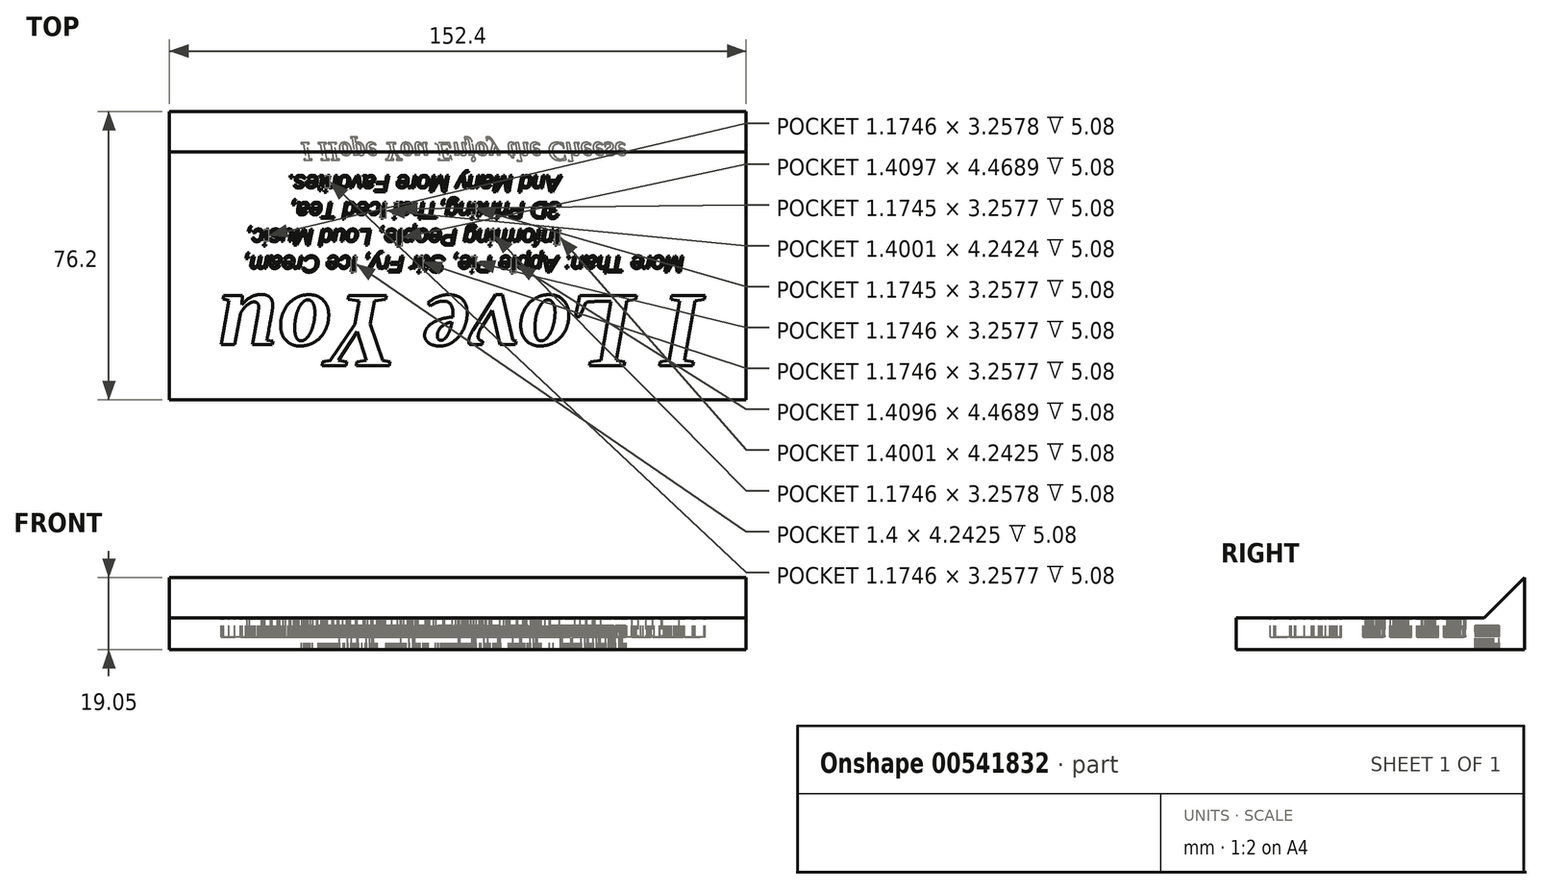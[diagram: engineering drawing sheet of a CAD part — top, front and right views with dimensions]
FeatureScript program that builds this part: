
annotation { "Feature Type Name" : "Feature", "Feature Type Description" : "" }
export const myFeature = defineFeature(function(context is Context, id is Id, definition is map)
    precondition{}
    {
        {
            var Q0;
            Q0=qCreatedBy(makeId("Top.planeOp"),FACE);
            var sketch = newSketch(context, id + "F0", { "sketchPlane" : qUnion([Q0])});
            skLineSegment(sketch, "E0", {"start": v(0, 0) * mm, "end": v(76.2, 0) * mm});
            skLineSegment(sketch, "E1", {"start": v(76.2, 0) * mm, "end": v(76.2, 76.2) * mm});
            skLineSegment(sketch, "E2", {"start": v(76.2, 76.2) * mm, "end": v(-76.2, 76.2) * mm});
            skLineSegment(sketch, "E3", {"start": v(-76.2, 76.2) * mm, "end": v(-76.2, 0) * mm});
            skLineSegment(sketch, "E4", {"start": v(-76.2, 0) * mm, "end": v(0, 0) * mm});
            skSolve(sketch);
        }
        {
            var Q0;
            Q0 = qSketchRegion(id + "F0", true);
            extrude(context, id + "F1", {"entities" : qUnion([Q0]), "depth" : 8.38 * mm, "offsetDistance" : 25.4 * mm});
        }
        {
            var Q0;
            Q0=makeQuery(id+"F1.opExtrude","SWEPT_FACE",FACE,{"disambiguationData":[OSD([sQuery(id+"F0.wireOp",EDGE,"E3")])]});
            var sketch = newSketch(context, id + "F2", { "sketchPlane" : qUnion([Q0])});
            skLineSegment(sketch, "E5", {"start": v(0, 0) * mm, "end": v(0, 19.05) * mm});
            skLineSegment(sketch, "E6", {"start": v(0, 19.05) * mm, "end": v(-19.05, 0) * mm});
            skLineSegment(sketch, "E7", {"start": v(-19.05, 0) * mm, "end": v(0, 0) * mm});
            skSolve(sketch);
        }
        {
            var Q0;
            Q0 = qSketchRegion(id + "F2", true);
            extrude(context, id + "F3", {"entities" : qUnion([Q0]), "operationType" : NewBodyOperationType.ADD, "oppositeDirection" : true, "depth" : 152.4 * mm, "offsetDistance" : 25.4 * mm});
        }
        {
            var Q0;
            Q0=makeQuery(id+"F1.opExtrude","CAP_FACE",FACE,{"disambiguationData":[OSD([sQuery(id+"F0.wireOp",EDGE,"E0"),sQuery(id+"F0.wireOp",EDGE,"E1"),sQuery(id+"F0.wireOp",EDGE,"E2"),sQuery(id+"F0.wireOp",EDGE,"E3"),sQuery(id+"F0.wireOp",EDGE,"E4")])],"isStart":false});
            var sketch = newSketch(context, id + "F4", { "sketchPlane" : qUnion([Q0])});
            skText(sketch, "E8", { "text": "I Love You", "fontName": "Tinos-BoldItalic.ttf"});
            const initialGuessF4  = {"E8": [-0.06505, 0.0487, 1, 0, 0.02032]};
            skSetInitialGuess(sketch, initialGuessF4);
            skSolve(sketch);
        }
        {
            var Q0;
            Q0 = qSketchRegion(id + "F4", true);
            extrude(context, id + "F5", {"entities" : qUnion([Q0]), "operationType" : NewBodyOperationType.REMOVE, "oppositeDirection" : true, "depth" : 5.08 * mm, "offsetDistance" : 25.4 * mm});
        }
        {
            var Q0;
            {var subQ0=sQuery(id+"F0.wireOp",EDGE,"E3");var subQ1=sQuery(id+"F0.wireOp",EDGE,"E2");var subQ5=sQuery(id+"F0.wireOp",EDGE,"E1");Q0=makeQuery(id+"F5.boolean.opBoolean","SPLIT",FACE,{"disambiguationData":[TD([makeQuery(id+"F1.opExtrude","SWEPT_FACE",FACE,{"disambiguationData":[OSD([subQ5])]})])],"derivedFrom":makeQuery(id+"F1.opExtrude","CAP_FACE",FACE,{"disambiguationData":[OSD([sQuery(id+"F0.wireOp",EDGE,"E0"),subQ5,subQ1,subQ0,sQuery(id+"F0.wireOp",EDGE,"E4")])],"isStart":false})});}
            var sketch = newSketch(context, id + "F6", { "sketchPlane" : qUnion([Q0])});
            skText(sketch, "E9", { "text": "More Than: Apple Pie, Stir Fry, Ice Cream,\n                   Informing People, Loud Music,\n                   3D Printing,Thai Iced Tea,\n                   And Many More Favorites.", "fontName": "Arimo-Italic.ttf"});
            const initialGuessF6  = {"E9": [-0.05977, 0.0382, 1, 0, 0.00444]};
            skSetInitialGuess(sketch, initialGuessF6);
            skSolve(sketch);
        }
        {
            var Q0;
            Q0 = qSketchRegion(id + "F6", true);
            extrude(context, id + "F7", {"entities" : qUnion([Q0]), "operationType" : NewBodyOperationType.REMOVE, "oppositeDirection" : true, "depth" : 5.08 * mm, "offsetDistance" : 25.4 * mm});
        }
        {
            var Q0;
            Q0=makeQuery(id+"F1.opExtrude","SWEPT_BODY",BODY,{"disambiguationData":[OSD([sQuery(id+"F0.wireOp",EDGE,"E0"),sQuery(id+"F0.wireOp",EDGE,"E1"),sQuery(id+"F0.wireOp",EDGE,"E2"),sQuery(id+"F0.wireOp",EDGE,"E3"),sQuery(id+"F0.wireOp",EDGE,"E4")])]});
            var Q1;
            Q1=makeQuery(id+"F3.boolean.opBoolean","MERGE",EDGE,{"derivedFrom":[makeQuery(id+"F1.opExtrude","SWEPT_EDGE",EDGE,{"disambiguationData":[OSD([sQuery(id+"F0.wireOp",EDGE,"E0"),sQuery(id+"F0.wireOp",EDGE,"E1")])]}),makeQuery(id+"F3.opExtrude","CAP_EDGE",EDGE,{"disambiguationData":[OSD([sQuery(id+"F2.wireOp",EDGE,"E5")])],"isStart":false})]});
            transform(context, id + "F8", {"entities" : qUnion([Q0]), "transformType" : TransformType.ROTATION, "transformAxis" : qUnion([Q1]), "angle" : 180 * degree, "makeCopy" : false});
        }
        {
            var Q0;
            Q0=makeQuery(id+"F1.opExtrude","CAP_FACE",FACE,{"disambiguationData":[OSD([sQuery(id+"F0.wireOp",EDGE,"E0"),sQuery(id+"F0.wireOp",EDGE,"E1"),sQuery(id+"F0.wireOp",EDGE,"E2"),sQuery(id+"F0.wireOp",EDGE,"E3"),sQuery(id+"F0.wireOp",EDGE,"E4")])],"isStart":true});
            var sketch = newSketch(context, id + "F9", { "sketchPlane" : qUnion([Q0])});
            skText(sketch, "E10", { "text": "I Hope You Enjoy the Cheese", "fontName": "Tinos-BoldItalic.ttf"});
            const initialGuessF9  = {"E10": [0.11097, 0.00825, 1, 0, 0.00508]};
            skSetInitialGuess(sketch, initialGuessF9);
            skSolve(sketch);
        }
        {
            var Q0;
            Q0 = qSketchRegion(id + "F9", true);
            extrude(context, id + "F10", {"entities" : qUnion([Q0]), "operationType" : NewBodyOperationType.REMOVE, "oppositeDirection" : true, "depth" : 6.35 * mm, "offsetDistance" : 25.4 * mm});
        }
    });
